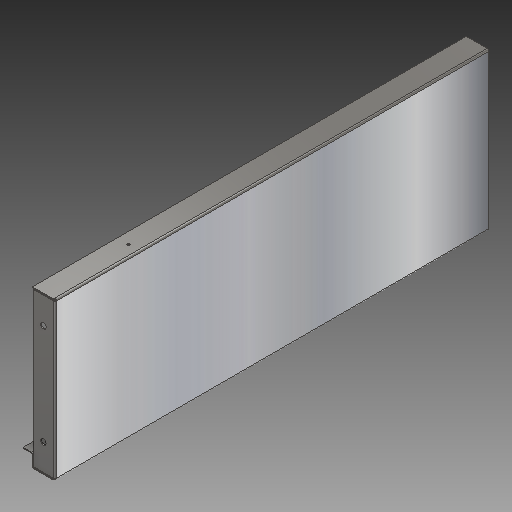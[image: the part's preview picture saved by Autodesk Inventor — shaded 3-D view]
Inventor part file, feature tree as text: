
AUTODESK INVENTOR PART (.ipt)
format: ipt  version: 2017 (Build 210142000, 142)  size: 335,360 bytes
history: native  units: mm
features: other x7, sketch x7, sheet_metal_op x6, extrude x4, reference x3, plane x1
ambient origin geometry x8: Origin, YZ Plane, XZ Plane, XY Plane, X Axis, Y Axis, Z Axis, Center Point
bodies: Solid1 (feature_tree)
feature tree (28):
  sheet_metal_op  "Contour Flange1"
  extrude  "Extrusion1"  Depth=40.0mm
  plane  "Work Plane1"
  other  "Decal1"
  extrude  "Extrusion2"  Depth=16.5mm
  extrude  "Extrusion3"  Depth=1.5mm
  sheet_metal_op  "Flange1"
  extrude  "Extrusion4"  Depth=1.5mm
  sketch  "Sketch1"  dims[d1=40.0mm d2=40.0mm]
  reference  "Reference1"
  reference  "Reference2"
  reference  "Reference3"
  other  "Plate1"
  sheet_metal_op  "Bend1"
  sheet_metal_op  "Corner1"
  sketch  "Sketch2"  dims[d3=22.0mm d4=16.5mm]
  sketch  "Sketch3"  dims[d5=1.5mm d6=0.75mm]
  other  "Image1"
  sketch  "Sketch4"  dims[d7=3.0mm d8=1.5mm]
  sketch  "Sketch5"  dims[d9=898.0mm]
  sketch  "Sketch6"  dims[d10=1.5mm]
  other  "Plate2"
  sheet_metal_op  "Bend2"
  sheet_metal_op  "Corner2"
  sketch  "Sketch7"  dims[d11=0.5mm d12=6.0mm d13=1.5mm d14=1.5mm d15=11.0mm d16=128.3mm d17=0.0mm d18=200.0mm d29=0.0mm d30=0.0mm d31=5.0mm d32=150.0mm d33=20.0mm d34=10.0mm d35=0.0mm d38=1.5mm d39=0.75mm d40=3.0mm d41=1.5mm d42=38.0mm d43=90.0deg d44=1.5mm d45=6.0mm d46=1.5mm d47=1.5mm d48=10.0mm d49=10.0mm d50=50.0mm d51=50.0mm d52=10.0mm d53=0.0mm]
  other  "Bancada de Lavagem Mãos - 1150 x 370 x 900h.iam"
  other  "Base:2"
  other  "Definition1"
